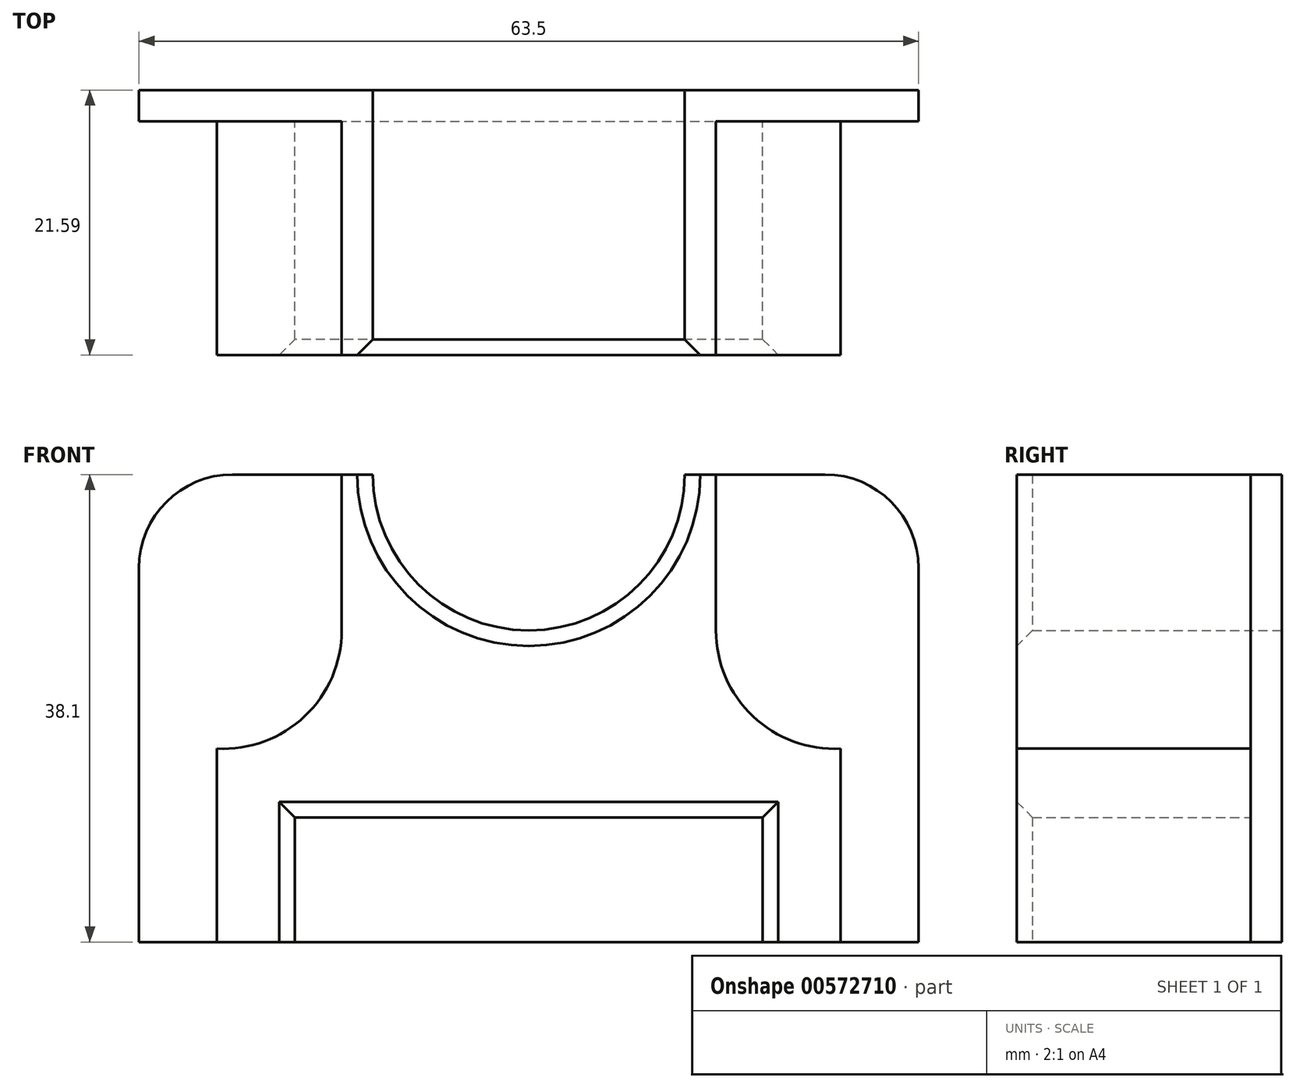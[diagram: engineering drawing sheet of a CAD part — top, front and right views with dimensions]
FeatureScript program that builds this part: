
annotation { "Feature Type Name" : "Feature", "Feature Type Description" : "" }
export const myFeature = defineFeature(function(context is Context, id is Id, definition is map)
    precondition{}
    {
        {
            var Q0;
            Q0=qCreatedBy(makeId("Front.planeOp"),FACE);
            var sketch = newSketch(context, id + "F0", { "sketchPlane" : qUnion([Q0])});
            skLineSegment(sketch, "E0.bottom", {"start": v(-31.75, 0) * mm, "end": v(31.75, 0) * mm});
            skLineSegment(sketch, "E0.top", {"start": v(-31.75, 38.1) * mm, "end": v(-12.7, 38.1) * mm});
            skLineSegment(sketch, "E0.left", {"start": v(-31.75, 0) * mm, "end": v(-31.75, 38.1) * mm});
            skLineSegment(sketch, "E0.right", {"start": v(31.75, 0) * mm, "end": v(31.75, 38.1) * mm});
            skArc(sketch, "E1", {"start": v(-12.7, 38.1) * mm, "mid": v(0, 25.4) * mm, "end": v(12.7, 38.1) * mm});
            skLineSegment(sketch, "E2.trimOffspring", {"start": v(12.7, 38.1) * mm, "end": v(31.75, 38.1) * mm});
            skSolve(sketch);
        }
        {
            var Q0;
            Q0 = qSketchRegion(id + "F0", true);
            extrude(context, id + "F1", {"entities" : qUnion([Q0]), "depth" : 2.54 * mm, "offsetDistance" : 25.4 * mm});
        }
        {
            var Q0;
            Q0=makeQuery(id+"F1.opExtrude","CAP_FACE",FACE,{"disambiguationData":[OSD([sQuery(id+"F0.wireOp",EDGE,"E0.bottom"),sQuery(id+"F0.wireOp",EDGE,"E0.top"),sQuery(id+"F0.wireOp",EDGE,"E0.left"),sQuery(id+"F0.wireOp",EDGE,"E0.right"),sQuery(id+"F0.wireOp",EDGE,"E1"),sQuery(id+"F0.wireOp",EDGE,"E2.trimOffspring")])],"isStart":false});
            var sketch = newSketch(context, id + "F2", { "sketchPlane" : qUnion([Q0])});
            skLineSegment(sketch, "E3", {"start": v(25.4, 0) * mm, "end": v(25.4, 15.76) * mm});
            skLineSegment(sketch, "E4", {"start": v(-25.4, 0) * mm, "end": v(-25.4, 15.76) * mm});
            skLineSegment(sketch, "E5", {"start": v(-15.24, 38.1) * mm, "end": v(-15.24, 25.4) * mm});
            skLineSegment(sketch, "E6", {"start": v(-15.24, 38.1) * mm, "end": v(-12.7, 38.1) * mm});
            skLineSegment(sketch, "E7", {"start": v(12.7, 38.1) * mm, "end": v(15.24, 38.1) * mm});
            skLineSegment(sketch, "E8", {"start": v(15.24, 38.1) * mm, "end": v(15.24, 25.4) * mm});
            skArc(sketch, "E9", {"start": v(15.24, 25.4) * mm, "mid": v(18.25, 18.4) * mm, "end": v(25.4, 15.76) * mm});
            skArc(sketch, "E10", {"start": v(-25.4, 15.76) * mm, "mid": v(-18.25, 18.4) * mm, "end": v(-15.24, 25.4) * mm});
            skArc(sketch, "E11.0", {"start": v(-12.7, 38.1) * mm, "mid": v(0, 25.4) * mm, "end": v(12.7, 38.1) * mm});
            skLineSegment(sketch, "E12", {"start": v(25.4, 0) * mm, "end": v(19.05, 0) * mm});
            skLineSegment(sketch, "E13", {"start": v(19.05, 0) * mm, "end": v(19.05, 10.16) * mm});
            skLineSegment(sketch, "E14", {"start": v(19.05, 10.16) * mm, "end": v(-19.05, 10.16) * mm});
            skLineSegment(sketch, "E15", {"start": v(-19.05, 10.16) * mm, "end": v(-19.05, 0) * mm});
            skLineSegment(sketch, "E16", {"start": v(-19.05, 0) * mm, "end": v(-25.4, 0) * mm});
            skSolve(sketch);
        }
        {
            var Q0;
            Q0 = qSketchRegion(id + "F2", true);
            extrude(context, id + "F3", {"entities" : qUnion([Q0]), "operationType" : NewBodyOperationType.ADD, "depth" : 19.05 * mm, "offsetDistance" : 25.4 * mm});
        }
        {
            var Q0;
            Q0=makeQuery(id+"F3.opExtrude","CAP_EDGE",EDGE,{"disambiguationData":[OSD([sQuery(id+"F2.wireOp",EDGE,"E14")])],"isStart":false});
            var Q1;
            Q1=makeQuery(id+"F3.opExtrude","CAP_EDGE",EDGE,{"disambiguationData":[OSD([sQuery(id+"F2.wireOp",EDGE,"E15")])],"isStart":false});
            var Q2;
            Q2=makeQuery(id+"F3.opExtrude","CAP_EDGE",EDGE,{"disambiguationData":[OSD([sQuery(id+"F2.wireOp",EDGE,"E13")])],"isStart":false});
            var Q3;
            Q3=makeQuery(id+"F3.opExtrude","CAP_EDGE",EDGE,{"disambiguationData":[OSD([sQuery(id+"F2.wireOp",EDGE,"E11.0")])],"isStart":false});
            chamfer(context, id + "F4", {"entities" : qUnion([Q0, Q1, Q2, Q3]), "width" : 1.27 * mm, "tangentPropagation" : true});
        }
        {
            var Q0;
            Q0=makeQuery(id+"F1.opExtrude","SWEPT_EDGE",EDGE,{"disambiguationData":[OSD([sQuery(id+"F0.wireOp",EDGE,"E0.top"),sQuery(id+"F0.wireOp",EDGE,"E0.left")])]});
            var Q1;
            Q1=makeQuery(id+"F1.opExtrude","SWEPT_EDGE",EDGE,{"disambiguationData":[OSD([sQuery(id+"F0.wireOp",EDGE,"E0.right"),sQuery(id+"F0.wireOp",EDGE,"E2.trimOffspring")])]});
            fillet(context, id + "F5", {"entities" : qUnion([Q0, Q1]), "radius" : 7.62 * mm, "tangentPropagation" : true, "allowEdgeOverflow" : false});
        }
    });
